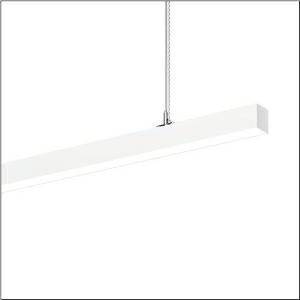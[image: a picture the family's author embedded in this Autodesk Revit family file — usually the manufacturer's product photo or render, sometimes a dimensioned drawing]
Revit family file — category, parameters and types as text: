
# Revit family: silica_r__21_51mx30da34wb_efde
name_source: partatom
category: Lighting Fixtures
units: mm (PartAtom-declared; Revit-internal decimal feet)

## family parameters
Cut with Voids When Loaded = No
Host = Face
Light Source = No
Part Type = Normal
Room Calculation Point = No
Round Connector Dimension = Use Diameter
Shared = No

## types (1)
- --- (1 x LED, 4210 lm, 27.7 W, 3000K)
    Apparent Load = 28 VA
    CIE Flux Codes = 47 79 96 57 100
    Color Rendering = 80
    Color Temperature = 3000K
    Default Elevation = 1800 mm
    Description = Silica® 21, office luminaire, primary optical cover: cover, of PMMA, opal, light emission: direct/indirect distribution, primary light characteristic: symmetric, installation type: suspended mounting, LED, rated luminous flux: 4.210lm, luminous efficacy: 152lm/W, light colour: 830, colour temperature: 3000K, control gear: DALI 2, with terminal, 3+2-pole, max. 2.5mm², mains connection: 220..240V, AC, 50/60Hz, rated input power: 27.7W, luminaire housing, of aluminium, traffic white (RAL 9016), length: 1.204mm, width: 53mm, height: 53mm, protection rating (complete): IP20, insulation class (complete): insulation class I (protective earthing), certification: CE, permissible operating ambient temperature: 0..+35°C, standard: EN 50419, packaging unit: 1 piece
    Height = 53 mm
    Lamp = 1 x LED
    Lamp Light Flux = 4210 lm
    Lamp Power = 27.7 W
    Lamp count = 1
    Length = 1204 mm
    Luminous efficacy = 152 lm/W
    Manufacturer = Siteco
    ModVariant = No
    Model = 51MX30DA34WB
    Mounting Place = Ceiling
    Mounting Type = Pendant
    Number of Poles = 1
    OnlyDefault = Yes
    Power Factor = 1
    Product Name = Silica® 21
    Product group = office luminaire | ceiling pendant
    ProductGroupID = 903
    Protection Class = Protection class I
    Protection Degree = IP 20
    RLX_Detail_Level = 1
    RLX_Emergency_Light_Flux = 0 lm
    RLX_Emergency_Type = 0
    RLX_Emergency_Type_DB = No
    RlxData = <blob elided: 20781 chars, md5=99c20eaa>
    Socket = socket
    Standby Power = 0 W
    System Light Flux = 4210 lm
    System Power = 28 W
    Type Comments = factory setting: luminous flux: 100 % | dim-lin: 254 | 233 mA
    Type Image = l_1349023.jpg
    URL = http://relux.com
    VarID = @adj_138995
    Voltage = 0 V
    Weight = 0.00 kg
    Width = 53 mm

## geometry (parser evidence)
native form markers: Blend x4, Sweep x12
no freeform markers — native parametric forms only
